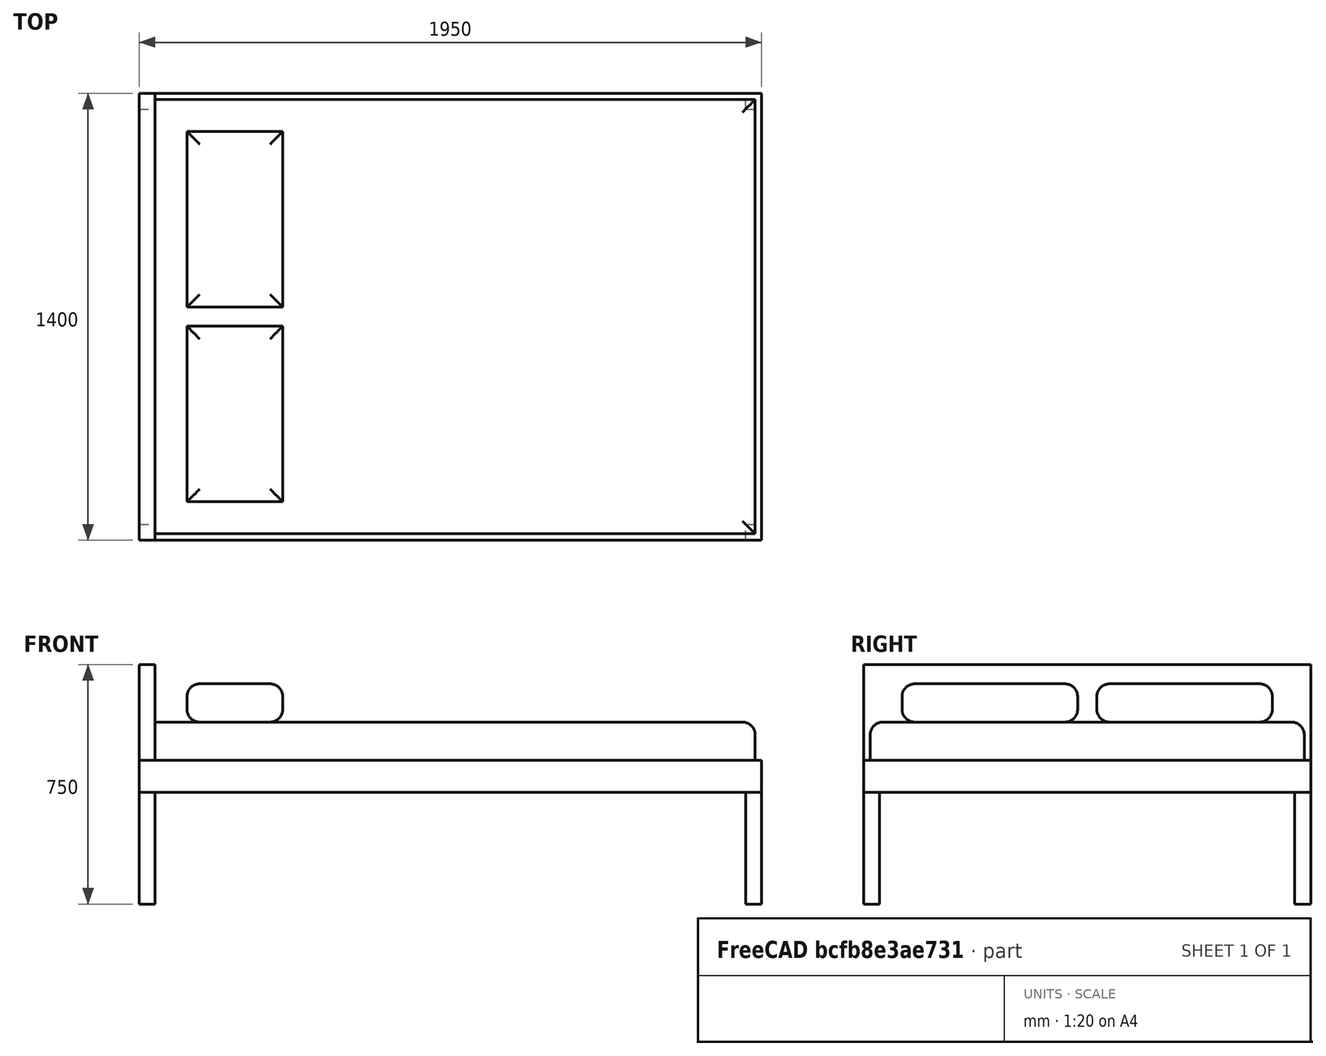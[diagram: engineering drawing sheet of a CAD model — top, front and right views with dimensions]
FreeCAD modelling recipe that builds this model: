
FCSTD DOCUMENT  (FreeCAD 0.17R8652 (Git))
Label: double bed 140x195cm
License: CreativeCommons Attribution
LicenseURL: http://creativecommons.org/licenses/by/4.0/
objects: Part::Box×9, Part::Fillet×3, Part::Compound×1
note: 13 computed .brp shape members not serialized (recipe doc carries the construction recipe); baked Part::Feature solids carry a one-line shape summary decoded from their .brp

FEATURE [Part::Box] Box  label="Cube"
  AttacherType = Attacher::AttachEngine3D
  Height = 350
  Length = 50
  Placement = pos=(0,1350,0) rot=(0,0,1;0rad)
  Width = 50
FEATURE [Part::Box] Box001  label="Cube001"
  AttacherType = Attacher::AttachEngine3D
  Height = 350
  Length = 50
  Width = 50
FEATURE [Part::Box] Box002  label="Cube002"
  AttacherType = Attacher::AttachEngine3D
  Height = 350
  Length = 50
  Placement = pos=(1900,0,0) rot=(0,0,1;0rad)
  Width = 50
FEATURE [Part::Box] Box003  label="Cube003"
  AttacherType = Attacher::AttachEngine3D
  Height = 350
  Length = 50
  Placement = pos=(1900,1350,0) rot=(0,0,1;0rad)
  Width = 50
FEATURE [Part::Box] Box004  label="Cube004"
  AttacherType = Attacher::AttachEngine3D
  Height = 100
  Length = 1950
  Placement = pos=(0,0,350) rot=(0,0,1;0rad)
  Width = 1400
FEATURE [Part::Box] Box005  label="Cube005"
  AttacherType = Attacher::AttachEngine3D
  Height = 120
  Length = 1880
  Placement = pos=(50,20,450) rot=(0,0,1;0rad)
  Width = 1360
FEATURE [Part::Box] Box006  label="Cube006"
  AttacherType = Attacher::AttachEngine3D
  Height = 300
  Length = 50
  Placement = pos=(0,0,450) rot=(0,0,1;0rad)
  Width = 1400
FEATURE [Part::Box] Box007  label="Cube007"
  AttacherType = Attacher::AttachEngine3D
  Height = 120
  Length = 300
  Placement = pos=(150,120,570) rot=(0,0,1;0rad)
  Width = 550
FEATURE [Part::Box] Box008  label="Cube008"
  AttacherType = Attacher::AttachEngine3D
  Height = 120
  Length = 300
  Placement = pos=(150,730,570) rot=(0,0,1;0rad)
  Width = 550
FEATURE [Part::Fillet] Fillet
  Base = -> Box005
  Edges = 3 edges r=40: [Edge6,Edge10,Edge12]
FEATURE [Part::Fillet] Fillet001
  Base = -> Box007
  Edges = 8 edges r=40: [Edge2,Edge4,Edge6,Edge8,Edge9,Edge10,Edge11,Edge12]
FEATURE [Part::Fillet] Fillet002
  Base = -> Box008
  Edges = 8 edges r=40: [Edge2,Edge4,Edge6,Edge8,Edge9,Edge10,Edge11,Edge12]
FEATURE [Part::Compound] Compound
  Links = -> [Box,Fillet,Fillet002,Box004,Fillet001,Box003,Box002,Box006,Box001]
